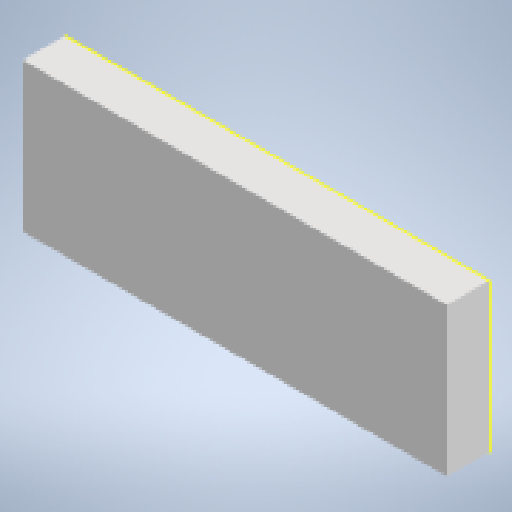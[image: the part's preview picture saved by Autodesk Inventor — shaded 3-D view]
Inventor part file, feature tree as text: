
AUTODESK INVENTOR PART (.ipt)
format: ipt  version: 2023 (Build 270158000, 158)  size: 127,488 bytes
history: native  units: mm
features: extrude x2, reference x2, sketch x1, other x1
ambient origin geometry x8: Origin, YZ Plane, XZ Plane, XY Plane, X Axis, Y Axis, Z Axis, Center Point
bodies: Body1 (feature_tree)
feature tree (6):
  sketch  "Sketch5"  dims[d12=2.0mm d13=0.0mm d14=2.0mm d15=0.0mm]
  extrude  "Extrusion7"  Depth=2.0mm TaperAngle=0.0deg
  extrude  "Extrusion8"  [1 undecoded]
  reference  "Reference4"
  reference  "Reference5"
  other  "3D_skenner.iam"
note: 1 required parameter value undecoded (feature->parameter linkage not recoverable at this tier; creation-order binding heuristic only, values carry confidence <= 0.55)
